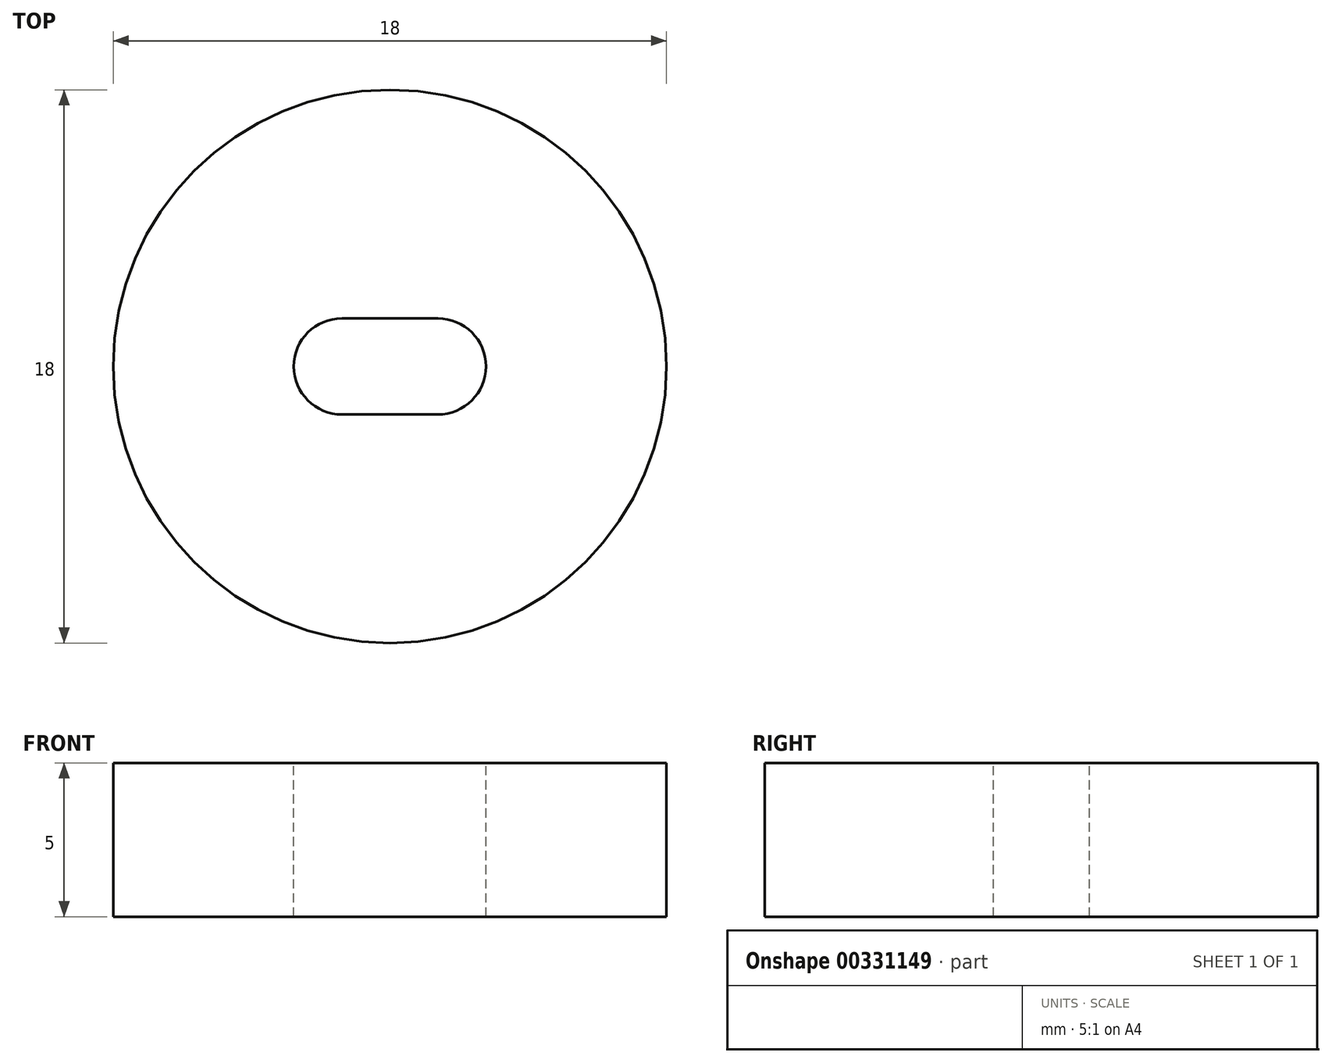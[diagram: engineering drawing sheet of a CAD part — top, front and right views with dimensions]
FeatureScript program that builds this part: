
annotation { "Feature Type Name" : "Feature", "Feature Type Description" : "" }
export const myFeature = defineFeature(function(context is Context, id is Id, definition is map)
    precondition{}
    {
        {
            var Q0;
            Q0=qCreatedBy(makeId("Top.planeOp"),FACE);
            var sketch = newSketch(context, id + "F0", { "sketchPlane" : qUnion([Q0])});
            skCircle(sketch, "E0", {"center": v(0, 0) * mm, "radius": 9 * mm});
            skSolve(sketch);
        }
        {
            var Q0;
            Q0 = qSketchRegion(id + "F0", true);
            extrude(context, id + "F1", {"entities" : qUnion([Q0]), "depth" : 5 * mm});
        }
        {
            var Q0;
            Q0=makeQuery(id+"F1.opExtrude","CAP_FACE",FACE,{"disambiguationData":[OSD([sQuery(id+"F0.wireOp",EDGE,"E0")])],"isStart":false});
            var sketch = newSketch(context, id + "F2", { "sketchPlane" : qUnion([Q0])});
            skCircle(sketch, "E1", {"center": v(0, 0) * mm, "radius": 6 * mm});
            skSolve(sketch);
        }
        {
            var Q0;
            Q0=makeQuery(id+"F2.imprint","IMPRINT",FACE,{"disambiguationData":[TD([[makeQuery(id+"F2.imprint","IMPRINT",EDGE,{"derivedFrom":sQuery(id+"F2.wireOp",EDGE,"E1")}),1.0]])]});
            var sketch = newSketch(context, id + "F3", { "sketchPlane" : qUnion([Q0])});
            skPoint(sketch, "E2.endSnap0", {"position": v(0.78, 0) * mm});
            skArc(sketch, "E3", {"start": v(1.56, -1.56) * mm, "mid": v(3.12, 0) * mm, "end": v(1.56, 1.56) * mm});
            skArc(sketch, "E4", {"start": v(-1.56, 1.56) * mm, "mid": v(-3.12, 0) * mm, "end": v(-1.56, -1.56) * mm});
            skLineSegment(sketch, "E5", {"start": v(-1.56, -1.56) * mm, "end": v(1.56, -1.56) * mm});
            skLineSegment(sketch, "E6", {"start": v(1.56, 1.56) * mm, "end": v(-1.56, 1.56) * mm});
            skSolve(sketch);
        }
        {
            var Q0;
            Q0=makeQuery(id+"F3.imprint","IMPRINT",FACE,{"disambiguationData":[TD([[makeQuery(id+"F3.imprint","IMPRINT",EDGE,{"derivedFrom":sQuery(id+"F3.wireOp",EDGE,"E3")}),1.0]])]});
            extrude(context, id + "F4", {"entities" : qUnion([Q0]), "operationType" : NewBodyOperationType.REMOVE, "oppositeDirection" : true, "depth" : 25 * mm});
        }
    });
